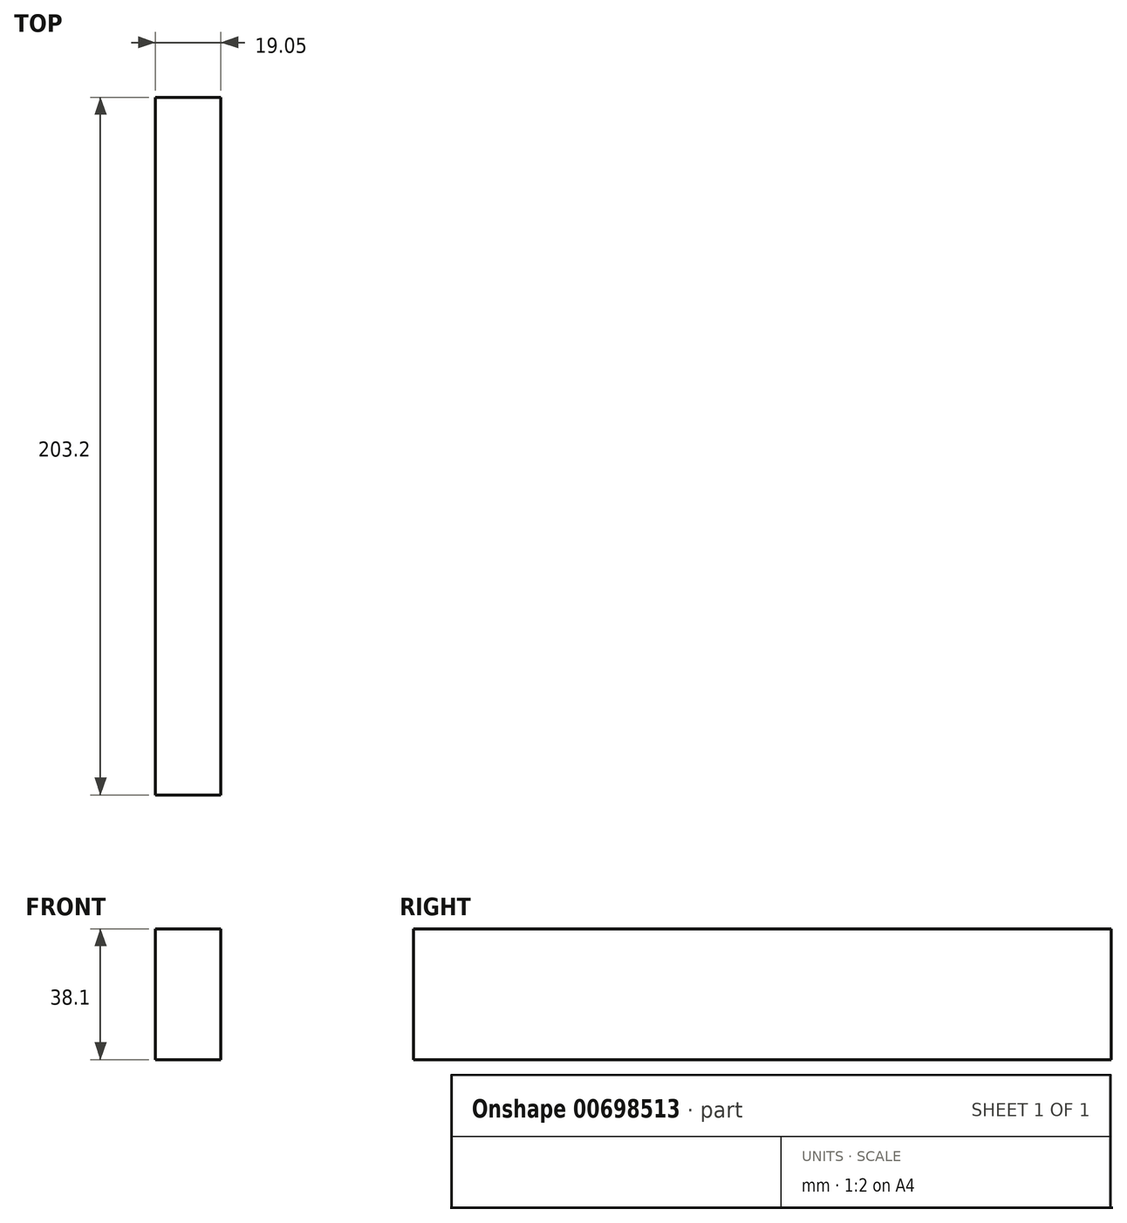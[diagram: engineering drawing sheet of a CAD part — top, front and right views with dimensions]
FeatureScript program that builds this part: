
annotation { "Feature Type Name" : "Feature", "Feature Type Description" : "" }
export const myFeature = defineFeature(function(context is Context, id is Id, definition is map)
    precondition{}
    {
        {
            var Q0;
            Q0=qCreatedBy(makeId("Right.planeOp"),FACE);
            var sketch = newSketch(context, id + "F0", { "sketchPlane" : qUnion([Q0])});
            skLineSegment(sketch, "E0.bottom", {"start": v(-98.33, -23.34) * mm, "end": v(104.87, -23.34) * mm});
            skLineSegment(sketch, "E0.top", {"start": v(-98.33, -61.44) * mm, "end": v(104.87, -61.44) * mm});
            skLineSegment(sketch, "E0.left", {"start": v(-98.33, -23.34) * mm, "end": v(-98.33, -61.44) * mm});
            skLineSegment(sketch, "E0.right", {"start": v(104.87, -23.34) * mm, "end": v(104.87, -61.44) * mm});
            skSolve(sketch);
        }
        {
            var Q0;
            Q0 = qSketchRegion(id + "F0", true);
            extrude(context, id + "F1", {"entities" : qUnion([Q0]), "depth" : 19.05 * mm, "offsetDistance" : 25.4 * mm});
        }
    });
